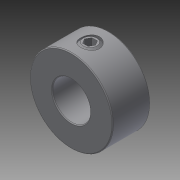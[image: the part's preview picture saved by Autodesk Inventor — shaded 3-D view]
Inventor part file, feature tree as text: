
AUTODESK INVENTOR PART (.ipt)
format: ipt  version: 2015 (Build 190159000, 159)  size: 161,792 bytes
history: native  units: in
note: dims shown in document units (in); Inventor stores cm internally (conversion verified against a paired STEP export)
features: other x2, imported_body x2, fillet x1
ambient origin geometry x8: Origin, YZ Plane, XZ Plane, XY Plane, X Axis, Y Axis, Z Axis, Center Point
bodies: Body1 (feature_tree), Body2 (feature_tree)
feature tree (5):
  fillet  "Fillet1"  [1 undecoded]
  other  "57485K6801"
  other  "Cut-Extrude2"
  imported_body  "Base1"
  imported_body  "Base2"
note: 1 required parameter value undecoded (feature->parameter linkage not recoverable at this tier; creation-order binding heuristic only, values carry confidence <= 0.55)
